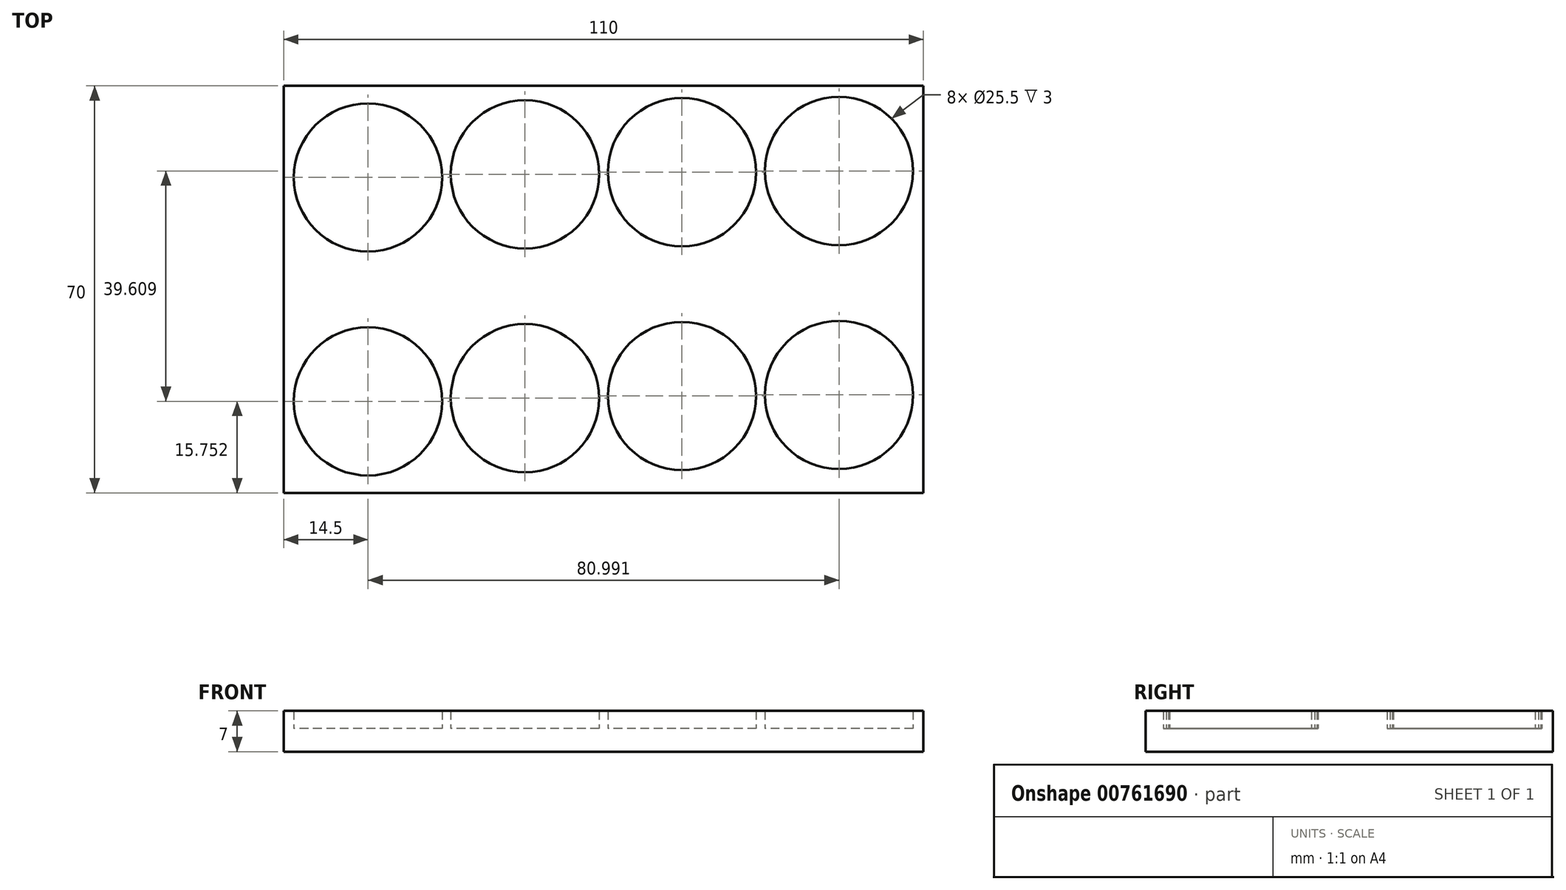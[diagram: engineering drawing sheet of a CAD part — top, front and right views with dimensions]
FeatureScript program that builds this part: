
annotation { "Feature Type Name" : "Feature", "Feature Type Description" : "" }
export const myFeature = defineFeature(function(context is Context, id is Id, definition is map)
    precondition{}
    {
        {
            var Q0;
            Q0=qCreatedBy(makeId("Top.planeOp"),FACE);
            var sketch = newSketch(context, id + "F0", { "sketchPlane" : qUnion([Q0])});
            skCircle(sketch, "E0", {"center": v(-40.5, 14.27) * mm, "radius": 12.75 * mm});
            skLineSegment(sketch, "E1.bottom", {"start": v(55, -1.48) * mm, "end": v(-55, -1.48) * mm});
            skLineSegment(sketch, "E1.top", {"start": v(55, 68.52) * mm, "end": v(-55, 68.52) * mm});
            skLineSegment(sketch, "E1.left", {"start": v(55, -1.48) * mm, "end": v(55, 68.52) * mm});
            skLineSegment(sketch, "E1.right", {"start": v(-55, -1.48) * mm, "end": v(-55, 68.52) * mm});
            skPoint(sketch, "E1.middle", {"position": v(0, 33.52) * mm});
            skCircle(sketch, "E2", {"center": v(13.5, 15.19) * mm, "radius": 12.75 * mm});
            skCircle(sketch, "E3", {"center": v(-13.5, 14.82) * mm, "radius": 12.75 * mm});
            skCircle(sketch, "E4", {"center": v(40.5, 15.38) * mm, "radius": 12.75 * mm});
            skCircle(sketch, "E5", {"center": v(-40.5, 52.77) * mm, "radius": 12.75 * mm});
            skCircle(sketch, "E6", {"center": v(13.5, 53.69) * mm, "radius": 12.75 * mm});
            skCircle(sketch, "E7", {"center": v(-13.5, 53.32) * mm, "radius": 12.75 * mm});
            skCircle(sketch, "E8", {"center": v(40.5, 53.88) * mm, "radius": 12.75 * mm});
            skSolve(sketch);
        }
        {
            var Q0;
            Q0=makeQuery(id+"F0.imprint","IMPRINT",FACE,{"disambiguationData":[TD([[makeQuery(id+"F0.imprint","IMPRINT",EDGE,{"derivedFrom":sQuery(id+"F0.wireOp",EDGE,"E0")}),-1.0]])]});
            extrude(context, id + "F1", {"entities" : qUnion([Q0]), "depth" : 7 * mm, "offsetDistance" : 25 * mm});
        }
        {
            var Q0;
            Q0=makeQuery(id+"F0.imprint","IMPRINT",FACE,{"disambiguationData":[TD([[makeQuery(id+"F0.imprint","IMPRINT",EDGE,{"derivedFrom":sQuery(id+"F0.wireOp",EDGE,"E5")}),1.0]])]});
            var Q1;
            Q1=makeQuery(id+"F0.imprint","IMPRINT",FACE,{"disambiguationData":[TD([[makeQuery(id+"F0.imprint","IMPRINT",EDGE,{"derivedFrom":sQuery(id+"F0.wireOp",EDGE,"E7")}),1.0]])]});
            var Q2;
            Q2=makeQuery(id+"F0.imprint","IMPRINT",FACE,{"disambiguationData":[TD([[makeQuery(id+"F0.imprint","IMPRINT",EDGE,{"derivedFrom":sQuery(id+"F0.wireOp",EDGE,"E6")}),1.0]])]});
            var Q3;
            Q3=makeQuery(id+"F0.imprint","IMPRINT",FACE,{"disambiguationData":[TD([[makeQuery(id+"F0.imprint","IMPRINT",EDGE,{"derivedFrom":sQuery(id+"F0.wireOp",EDGE,"E8")}),1.0]])]});
            var Q4;
            Q4=makeQuery(id+"F0.imprint","IMPRINT",FACE,{"disambiguationData":[TD([[makeQuery(id+"F0.imprint","IMPRINT",EDGE,{"derivedFrom":sQuery(id+"F0.wireOp",EDGE,"E4")}),1.0]])]});
            var Q5;
            Q5=makeQuery(id+"F0.imprint","IMPRINT",FACE,{"disambiguationData":[TD([[makeQuery(id+"F0.imprint","IMPRINT",EDGE,{"derivedFrom":sQuery(id+"F0.wireOp",EDGE,"E2")}),1.0]])]});
            var Q6;
            Q6=makeQuery(id+"F0.imprint","IMPRINT",FACE,{"disambiguationData":[TD([[makeQuery(id+"F0.imprint","IMPRINT",EDGE,{"derivedFrom":sQuery(id+"F0.wireOp",EDGE,"E3")}),1.0]])]});
            var Q7;
            Q7=makeQuery(id+"F0.imprint","IMPRINT",FACE,{"disambiguationData":[TD([[makeQuery(id+"F0.imprint","IMPRINT",EDGE,{"derivedFrom":sQuery(id+"F0.wireOp",EDGE,"E0")}),1.0]])]});
            extrude(context, id + "F2", {"entities" : qUnion([Q0, Q1, Q2, Q3, Q4, Q5, Q6, Q7]), "operationType" : NewBodyOperationType.ADD, "depth" : 4 * mm, "offsetDistance" : 25 * mm});
        }
    });
